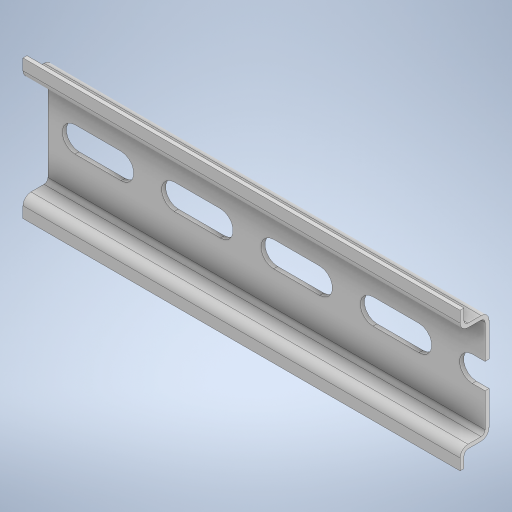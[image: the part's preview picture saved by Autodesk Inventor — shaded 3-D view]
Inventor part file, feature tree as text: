
AUTODESK INVENTOR PART (.ipt)
format: ipt  version: 2023 (Build 270158030, 158C)  size: 390,656 bytes
history: native  units: mm
features: other x4, extrude x3, sketch x3, reference x1
ambient origin geometry x8: Origin, YZ Plane, XZ Plane, XY Plane, X Axis, Y Axis, Z Axis, Center Point
bodies: Body1 (feature_tree)
feature tree (11):
  other  "DIN"
  extrude  "Extrusion1"  Depth=1.0mm
  extrude  "Extrusion2"  Depth=7.3mm
  extrude  "Extrusion3"  Depth=1.0mm
  sketch  "Sketch1"  dims[d0=1.0mm d1=1.0mm]
  reference  "Reference1"
  sketch  "Sketch2"  dims[d5=35.0mm d8=7.3mm]
  sketch  "Sketch3"  dims[d9=1.0mm d10=1.0mm d11=2.0mm d12=2.0mm d13=12.7mm d15=12.7mm d16=4.8mm d17=4.8mm d20=1.0mm d21=1.0mm d22=2.0mm d23=300.0mm d24=0.0mm d26=18.0mm d31=80.0mm d33=25.0mm d34=10.0mm d36=10.0mm d39=25.0mm d40=0.0mm d46=3.6mm d47=17.5mm d48=17.5mm d49=50.0mm d51=25.0mm d52=10.0mm d54=10.0mm d56=110.0mm d57=2.0mm d58=5.0mm d59=5.0mm d60=0.0mm d61=0.0mm]
  other  "<userpath>\Documents\0004-inventor\Inventor_Projects\electronics-enclosure\enclosure.iam"
  other  "enclosure.iam"
  other  "assembly-board:1"
